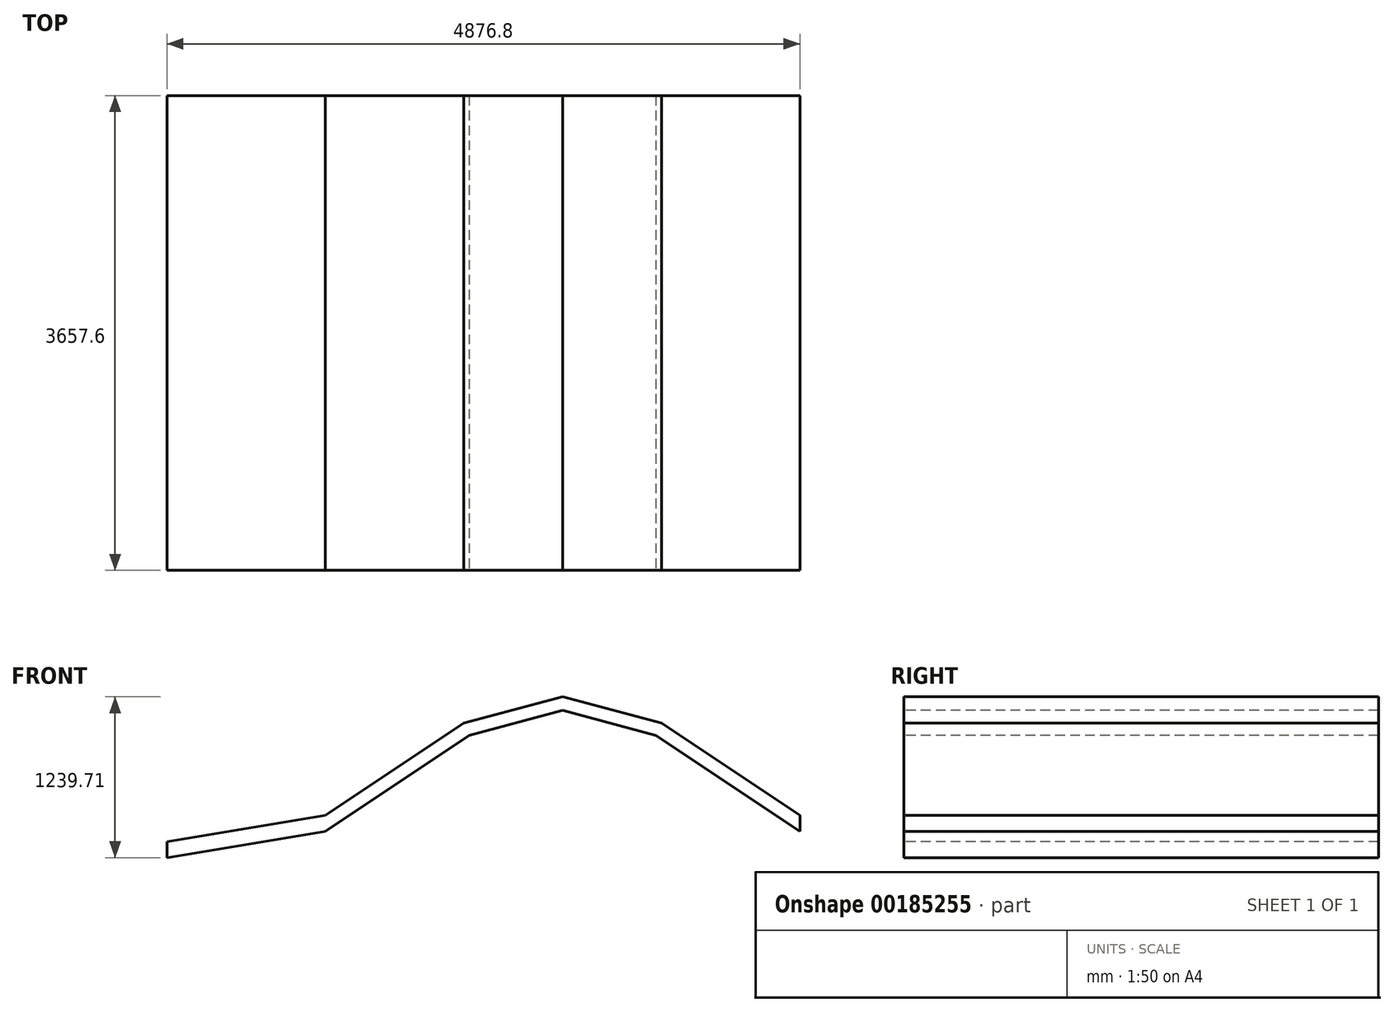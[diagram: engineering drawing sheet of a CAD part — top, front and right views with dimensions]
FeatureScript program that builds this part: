
annotation { "Feature Type Name" : "Feature", "Feature Type Description" : "" }
export const myFeature = defineFeature(function(context is Context, id is Id, definition is map)
    precondition{}
    {
        {
            var Q0;
            Q0=qCreatedBy(makeId("Front.planeOp"),FACE);
            var sketch = newSketch(context, id + "F0", { "sketchPlane" : qUnion([Q0])});
            skLineSegment(sketch, "E0", {"start": v(0, 3048) * mm, "end": v(0, 0) * mm, "construction": true});
            skLineSegment(sketch, "E1", {"start": v(0, 0) * mm, "end": v(-3048, 0) * mm, "construction": true});
            skLineSegment(sketch, "E2", {"start": v(0, 0) * mm, "end": v(3048, 0) * mm, "construction": true});
            skLineSegment(sketch, "E3.bottom", {"start": v(-1828.8, 3352.8) * mm, "end": v(1828.8, 3352.8) * mm, "construction": true});
            skLineSegment(sketch, "E3.top", {"start": v(-1828.8, 0) * mm, "end": v(1828.8, 0) * mm, "construction": true});
            skLineSegment(sketch, "E3.left", {"start": v(-1828.8, 3352.8) * mm, "end": v(-1828.8, 0) * mm, "construction": true});
            skLineSegment(sketch, "E3.right", {"start": v(1828.8, 3352.8) * mm, "end": v(1828.8, 0) * mm, "construction": true});
            skLineSegment(sketch, "E4", {"start": v(-1828.8, 2438.4) * mm, "end": v(1828.8, 2438.4) * mm, "construction": true});
            skLineSegment(sketch, "E5", {"start": v(0, 0) * mm, "end": v(0, 4368.8) * mm, "construction": true});
            skLineSegment(sketch, "E6", {"start": v(-762, 3149.6) * mm, "end": v(-762, 3149.6) * mm});
            skPoint(sketch, "E7", {"position": v(0, 3352.8) * mm});
            skLineSegment(sketch, "E8", {"start": v(-762, 3149.6) * mm, "end": v(0, 3352.8) * mm});
            skLineSegment(sketch, "E9", {"start": v(-762, 3149.6) * mm, "end": v(-1828.8, 2438.4) * mm});
            skLineSegment(sketch, "E10", {"start": v(-1828.8, 2438.4) * mm, "end": v(-3048, 2235.2) * mm});
            skLineSegment(sketch, "E11", {"start": v(-762, 3149.6) * mm, "end": v(0, 3149.6) * mm, "construction": true});
            skLineSegment(sketch, "E12.1", {"start": v(-719.6, 3055.75) * mm, "end": v(-1828.8, 2316.3) * mm});
            skLineSegment(sketch, "E13", {"start": v(-3048, 2235.2) * mm, "end": v(-3048, 2113.1) * mm});
            skLineSegment(sketch, "E14", {"start": v(0, 3352.8) * mm, "end": v(0, 3136.52) * mm, "construction": true});
            skLineSegment(sketch, "E15", {"start": v(-1828.8, 2316.3) * mm, "end": v(-3048, 2113.1) * mm});
            skLineSegment(sketch, "E16", {"start": v(-762, 3149.6) * mm, "end": v(-719.6, 3055.75) * mm, "construction": true});
            skLineSegment(sketch, "E17", {"start": v(-719.6, 3055.75) * mm, "end": v(0, 3247.65) * mm});
            skLineSegment(sketch, "E18.MirrorCS", {"start": v(719.6, 3055.75) * mm, "end": v(0, 3247.65) * mm});
            skLineSegment(sketch, "E19.MirrorCS", {"start": v(762, 3149.6) * mm, "end": v(0, 3352.8) * mm});
            skLineSegment(sketch, "E20.MirrorCS", {"start": v(719.6, 3055.75) * mm, "end": v(1828.8, 2316.3) * mm});
            skLineSegment(sketch, "E21.MirrorCS", {"start": v(762, 3149.6) * mm, "end": v(1828.8, 2438.4) * mm});
            skLineSegment(sketch, "E22", {"start": v(1828.8, 2438.4) * mm, "end": v(1828.8, 2316.3) * mm});
            skSolve(sketch);
        }
        {
            var Q0;
            Q0=sQuery(id+"F0.wireOp",EDGE,"E14");
            var Q1;
            Q1=sQuery(id+"F0.wireOp",EDGE,"E8");
            var Q2;
            Q2=sQuery(id+"F0.wireOp",EDGE,"E17");
            var Q3;
            Q3=sQuery(id+"F0.wireOp",EDGE,"E19.MirrorCS");
            var Q4;
            Q4=sQuery(id+"F0.wireOp",EDGE,"E12.1");
            var Q5;
            Q5=sQuery(id+"F0.wireOp",EDGE,"E9");
            var Q6;
            Q6=sQuery(id+"F0.wireOp",EDGE,"E10");
            var Q7;
            Q7=sQuery(id+"F0.wireOp",EDGE,"E15");
            var Q8;
            Q8=sQuery(id+"F0.wireOp",EDGE,"E21.MirrorCS");
            var Q9;
            Q9=sQuery(id+"F0.wireOp",EDGE,"E20.MirrorCS");
            var Q10;
            Q10=sQuery(id+"F0.wireOp",EDGE,"E22");
            var Q11;
            Q11=sQuery(id+"F0.wireOp",EDGE,"E13");
            var Q12;
            Q12=sQuery(id+"F0.wireOp",EDGE,"E18.MirrorCS");
            extrude(context, id + "F1", {"bodyType" : ToolBodyType.SURFACE, "surfaceEntities" : qUnion([Q0, Q1, Q2, Q3, Q4, Q5, Q6, Q7, Q8, Q9, Q10, Q11, Q12]), "depth" : 3657.6 * mm});
        }
    });
